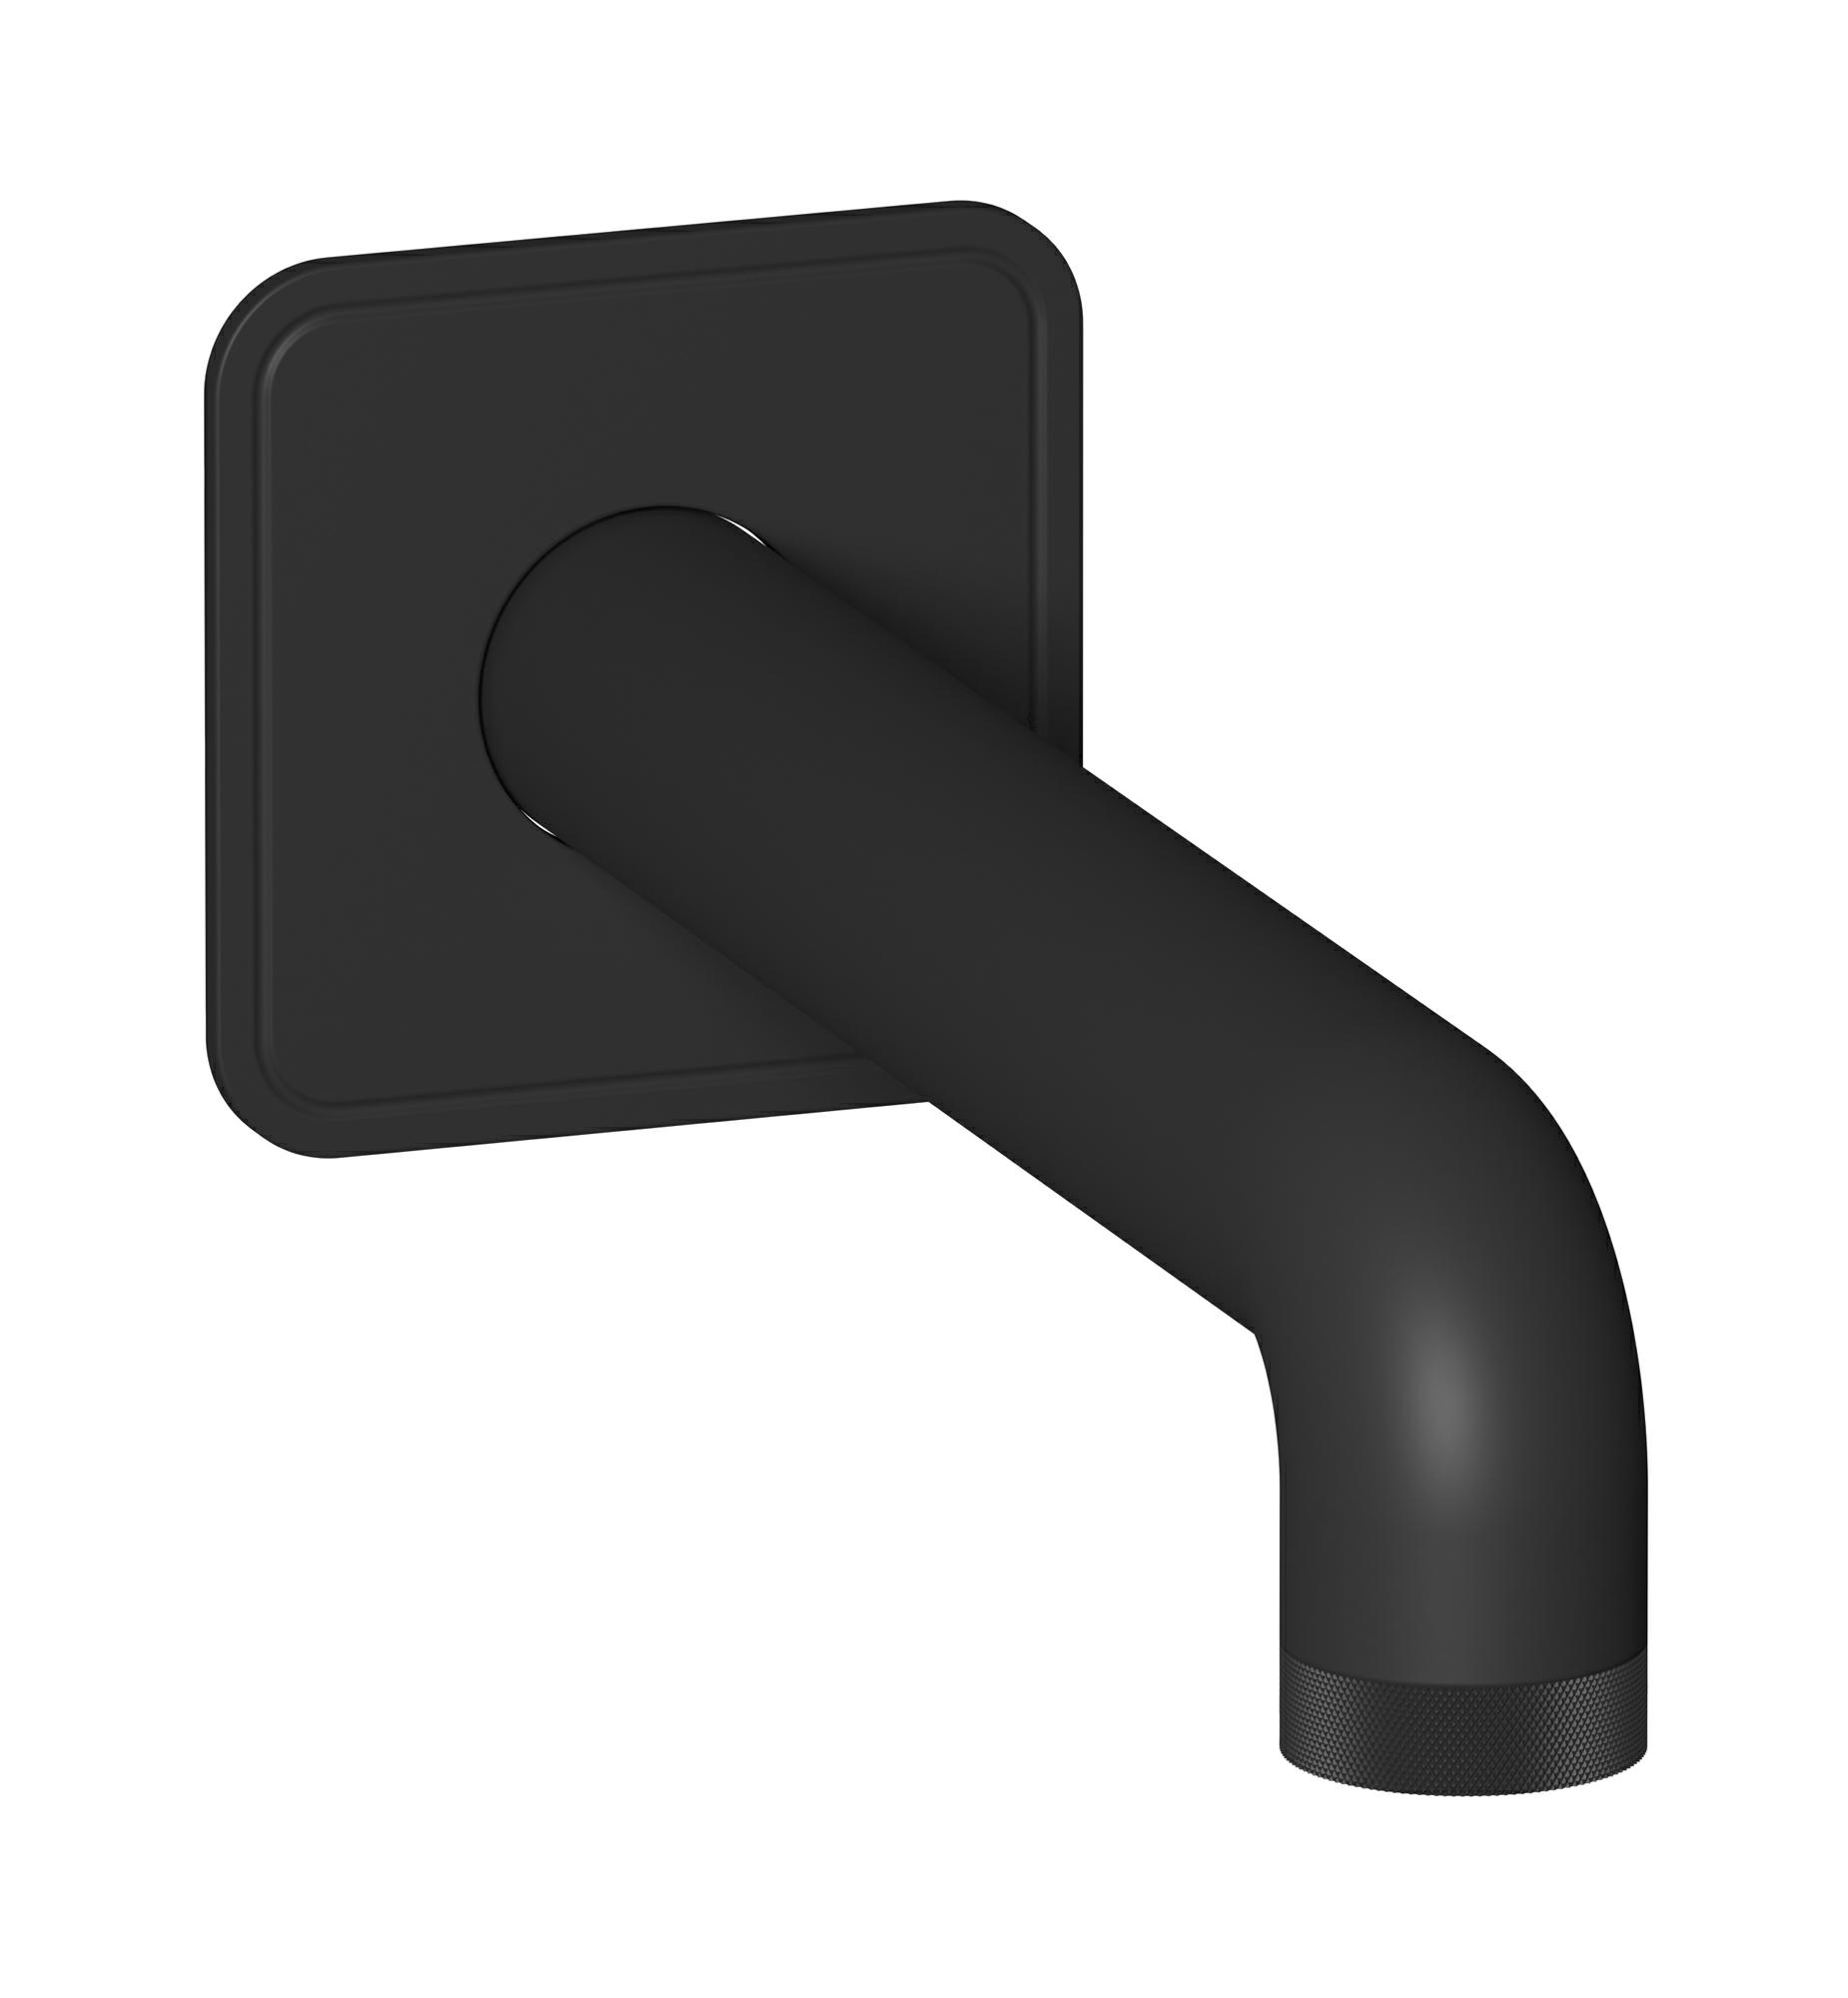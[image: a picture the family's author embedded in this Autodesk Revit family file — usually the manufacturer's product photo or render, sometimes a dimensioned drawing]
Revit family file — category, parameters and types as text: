
# Revit family: B2320_22
name_source: partatom
category: Apparecchi idraulici
units: mm (PartAtom-declared; Revit-internal decimal feet)

## family parameters
Basato su piano di lavoro = No
Condiviso = No
Mantieni orientamento annotazione = No
Numero OmniClass = 23.45.55.17
Punto di calcolo locali = No
Quota connettore circolare = Usa diametro
Sempre verticale = Sì
Taglio con vuoti quando caricato = No
Tipo di parte = Normale
Titolo OmniClass = Mixing Faucets

## types (13) — shared parameters
Commenti sul tipo = Wall spout with plate
Connessione CW = No
Connessione HW = No
Connessione di scarico = No
Connessione di ventilazione = No
Descrizione = Wall spout with plate
Produttore = IB Rubinetterie S.p.A.
URL = https://www.weareib.it
Water inlet = 10 mm  [stored 0.0328084 ft]
zero-valued in all types: Prospetto di default

## per-type parameters (varying)
| type | Finishes surface | Immagine tipo | Modello |
| Chrome | IB_Chrome | B2320CC_22.jpg | B2320CC_22 |
| Black Chrome | IB_Black chrome | B2320CF_22.jpg | B2320CF_22 |
| Brushed Black Chrome | IB_Brushed black chrome | B2320CS_22.jpg | B2320CS_22 |
| Pale Gold | IB_Pale gold | B2320II_22.jpg | B2320II_22 |
| Brushed Pale Gold | IB_brushed pale gold | B2320IS_22.jpg | B2320IS_22 |
| Modern Bronze | IB_Modern bronze | B2320MB_22.jpg | B2320MB_22 |
| Matt Black | IB_matt black | B2320NP_22.jpg | B2320NP_22 |
| Natural Brass | IB_Brass | B2320ON_22.jpg | B2320ON_22 |
| Gold | IB_gold | B2320OO_22.jpg | B2320OO_22 |
| Brushed Gold | IB_brushed gold | B2320OS_22.jpg | B2320OS_22 |
| Rose Gold | IB_Rose gold | B2320RS_22.jpg | B2320RS_22 |
| Brushed Rose Gold | IB_Brushed rose gold | B2320SR_22.jpg | B2320SR_22 |
| Brushed Nickel | IB_Brushed nickel | B2320SS_22.jpg | B2320SS_22 |

note: [stored X ft] marks values corroborated as IEEE doubles in the binary element streams (Revit-internal decimal feet)
